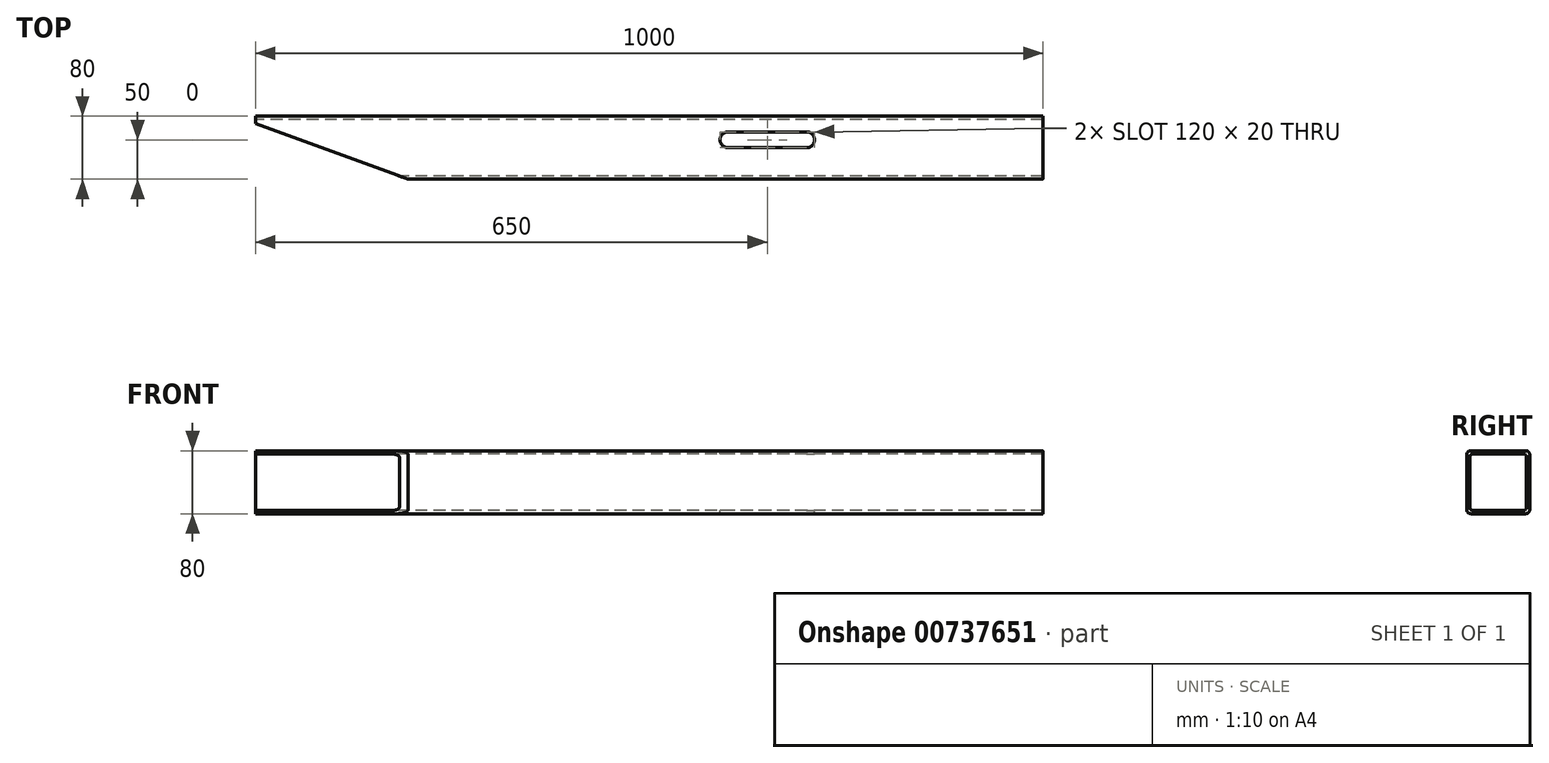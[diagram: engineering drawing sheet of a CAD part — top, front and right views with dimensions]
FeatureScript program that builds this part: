
annotation { "Feature Type Name" : "Feature", "Feature Type Description" : "" }
export const myFeature = defineFeature(function(context is Context, id is Id, definition is map)
    precondition{}
    {
        {
            var Q0;
            Q0=qCreatedBy(makeId("Right.planeOp"),FACE);
            var sketch = newSketch(context, id + "F0", { "sketchPlane" : qUnion([Q0])});
            skLineSegment(sketch, "E0.bottom", {"start": v(-35, 40) * mm, "end": v(35, 40) * mm});
            skLineSegment(sketch, "E0.top", {"start": v(-35, -40) * mm, "end": v(35, -40) * mm});
            skLineSegment(sketch, "E0.left", {"start": v(-40, 35) * mm, "end": v(-40, -35) * mm});
            skLineSegment(sketch, "E0.right", {"start": v(40, 35) * mm, "end": v(40, -35) * mm});
            skLineSegment(sketch, "E1.bottom", {"start": v(-32, 36) * mm, "end": v(32, 36) * mm});
            skLineSegment(sketch, "E1.top", {"start": v(-32, -36) * mm, "end": v(32, -36) * mm});
            skLineSegment(sketch, "E1.left", {"start": v(-36, 32) * mm, "end": v(-36, -32) * mm});
            skLineSegment(sketch, "E1.right", {"start": v(36, 32) * mm, "end": v(36, -32) * mm});
            skPoint(sketch, "E2.visualSharp", {"position": v(-36, 36) * mm});
            skArc(sketch, "E2.filletArc", {"start": v(-32, 36) * mm, "mid": v(-34.83, 34.83) * mm, "end": v(-36, 32) * mm});
            skPoint(sketch, "E3.visualSharp", {"position": v(-36, -36) * mm});
            skArc(sketch, "E3.filletArc", {"start": v(-36, -32) * mm, "mid": v(-34.83, -34.83) * mm, "end": v(-32, -36) * mm});
            skPoint(sketch, "E4.visualSharp", {"position": v(36, -36) * mm});
            skArc(sketch, "E4.filletArc", {"start": v(32, -36) * mm, "mid": v(34.83, -34.83) * mm, "end": v(36, -32) * mm});
            skPoint(sketch, "E5.visualSharp", {"position": v(36, 36) * mm});
            skArc(sketch, "E5.filletArc", {"start": v(36, 32) * mm, "mid": v(34.83, 34.83) * mm, "end": v(32, 36) * mm});
            skPoint(sketch, "E6.visualSharp", {"position": v(-40, 40) * mm});
            skArc(sketch, "E6.filletArc", {"start": v(-35, 40) * mm, "mid": v(-38.54, 38.54) * mm, "end": v(-40, 35) * mm});
            skPoint(sketch, "E7.visualSharp", {"position": v(-40, -40) * mm});
            skArc(sketch, "E7.filletArc", {"start": v(-40, -35) * mm, "mid": v(-38.54, -38.54) * mm, "end": v(-35, -40) * mm});
            skPoint(sketch, "E8.visualSharp", {"position": v(40, -40) * mm});
            skArc(sketch, "E8.filletArc", {"start": v(35, -40) * mm, "mid": v(38.54, -38.54) * mm, "end": v(40, -35) * mm});
            skPoint(sketch, "E9.visualSharp", {"position": v(40, 40) * mm});
            skArc(sketch, "E9.filletArc", {"start": v(40, 35) * mm, "mid": v(38.54, 38.54) * mm, "end": v(35, 40) * mm});
            skSolve(sketch);
        }
        {
            var Q0;
            Q0=makeQuery(id+"F0.imprint","IMPRINT",FACE,{"disambiguationData":[TD([[makeQuery(id+"F0.imprint","IMPRINT",EDGE,{"derivedFrom":sQuery(id+"F0.wireOp",EDGE,"E0.bottom")}),-1.0]])]});
            extrude(context, id + "F1", {"entities" : qUnion([Q0]), "endBound" : BoundingType.SYMMETRIC, "depth" : 1000 * mm, "offsetDistance" : 25 * mm});
        }
        {
            var Q0;
            Q0=makeQuery(id+"F1.opExtrude","SWEPT_FACE",FACE,{"disambiguationData":[OSD([sQuery(id+"F0.wireOp",EDGE,"E0.bottom")])]});
            var sketch = newSketch(context, id + "F2", { "sketchPlane" : qUnion([Q0])});
            skLineSegment(sketch, "E10", {"start": v(-540, 45) * mm, "end": v(-265.45, -54.93) * mm});
            skLineSegment(sketch, "E11", {"start": v(-265.45, -54.93) * mm, "end": v(-540, -54.93) * mm});
            skLineSegment(sketch, "E12", {"start": v(-540, -54.93) * mm, "end": v(-540, 45) * mm});
            skLineSegment(sketch, "E13.0", {"start": v(-500, -35) * mm, "end": v(-500, 35) * mm});
            skLineSegment(sketch, "E14.0", {"start": v(500, -35) * mm, "end": v(-500, -35) * mm});
            skSolve(sketch);
        }
        {
            var Q0;
            {var subQ1=sQuery(id+"F2.wireOp",EDGE,"E11");Q0=makeQuery(id+"F2.imprint","IMPRINT",FACE,{"disambiguationData":[TD([[makeQuery(id+"F2.imprint","IMPRINT",EDGE,{"derivedFrom":subQ1}),-1.0]])]});}
            var Q1;
            {var subQ0=sQuery(id+"F2.wireOp",EDGE,"E13.0");var subQ1=sQuery(id+"F2.wireOp",EDGE,"E10");var subQ2=makeQuery(id+"F2.imprint","INTERSECT",VERTEX,{"derivedFrom":[subQ1,subQ0]});Q1=makeQuery(id+"F2.imprint","IMPRINT",FACE,{"disambiguationData":[TD([[makeQuery(id+"F2.imprint","IMPRINT",EDGE,{"disambiguationData":[TD([[subQ2,-1.0]])],"derivedFrom":subQ1}),-1.0]])]});}
            var Q2;
            Q2=makeQuery(id+"F1.opExtrude","SWEPT_FACE",FACE,{"disambiguationData":[OSD([sQuery(id+"F0.wireOp",EDGE,"E0.top")])]});
            extrude(context, id + "F3", {"entities" : qUnion([Q0, Q1]), "operationType" : NewBodyOperationType.REMOVE, "endBound" : BoundingType.UP_TO_SURFACE, "oppositeDirection" : true, "depth" : 25 * mm, "endBoundEntityFace" : qUnion([Q2]), "offsetDistance" : 25 * mm});
        }
        {
            var Q0;
            Q0=makeQuery(id+"F1.opExtrude","SWEPT_FACE",FACE,{"disambiguationData":[OSD([sQuery(id+"F0.wireOp",EDGE,"E0.bottom")])]});
            var sketch = newSketch(context, id + "F4", { "sketchPlane" : qUnion([Q0])});
            skArc(sketch, "E15", {"start": v(200, 0) * mm, "mid": v(210, 10) * mm, "end": v(200, 20) * mm});
            skArc(sketch, "E16", {"start": v(100, 20) * mm, "mid": v(90, 10) * mm, "end": v(100, 0) * mm});
            skLineSegment(sketch, "E17", {"start": v(200, 0) * mm, "end": v(100, 0) * mm});
            skLineSegment(sketch, "E18", {"start": v(200, 20) * mm, "end": v(100, 20) * mm});
            skSolve(sketch);
        }
        {
            var Q0;
            Q0=makeQuery(id+"F4.imprint","IMPRINT",FACE,{"disambiguationData":[TD([[makeQuery(id+"F4.imprint","IMPRINT",EDGE,{"derivedFrom":sQuery(id+"F4.wireOp",EDGE,"E15")}),1.0]])]});
            extrude(context, id + "F5", {"entities" : qUnion([Q0]), "operationType" : NewBodyOperationType.REMOVE, "endBound" : BoundingType.THROUGH_ALL, "oppositeDirection" : true, "depth" : 25 * mm, "offsetDistance" : 25 * mm});
        }
    });
